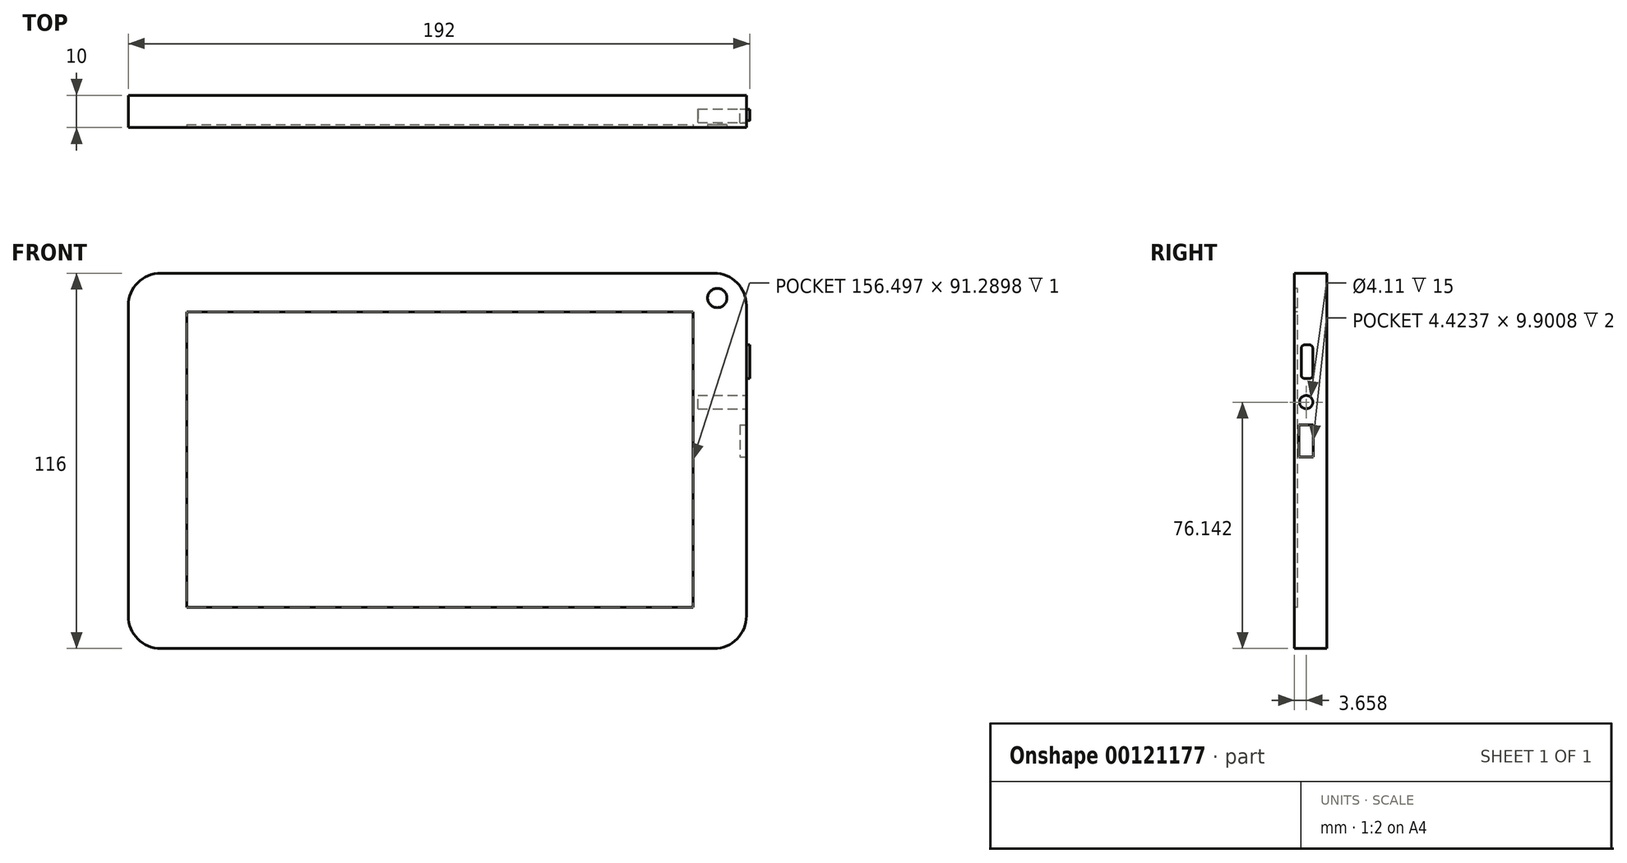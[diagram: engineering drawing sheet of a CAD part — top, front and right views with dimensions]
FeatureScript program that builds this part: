
annotation { "Feature Type Name" : "Feature", "Feature Type Description" : "" }
export const myFeature = defineFeature(function(context is Context, id is Id, definition is map)
    precondition{}
    {
        {
            var Q0;
            Q0=qCreatedBy(makeId("Front.planeOp"),FACE);
            var sketch = newSketch(context, id + "F0", { "sketchPlane" : qUnion([Q0])});
            skLineSegment(sketch, "E0.bottom", {"start": v(-85.5, 58) * mm, "end": v(85.5, 58) * mm});
            skLineSegment(sketch, "E0.top", {"start": v(-85.5, -58) * mm, "end": v(85.5, -58) * mm});
            skLineSegment(sketch, "E0.left", {"start": v(-95.5, 48) * mm, "end": v(-95.5, -48) * mm});
            skLineSegment(sketch, "E0.right", {"start": v(95.5, 48) * mm, "end": v(95.5, -48) * mm});
            skPoint(sketch, "E0.middle", {"position": v(0, 0) * mm});
            skPoint(sketch, "E1.visualSharp", {"position": v(-95.5, 58) * mm});
            skArc(sketch, "E1.filletArc", {"start": v(-85.5, 58) * mm, "mid": v(-92.57, 55.07) * mm, "end": v(-95.5, 48) * mm});
            skPoint(sketch, "E2.visualSharp", {"position": v(-95.5, -58) * mm});
            skArc(sketch, "E2.filletArc", {"start": v(-95.5, -48) * mm, "mid": v(-92.57, -55.07) * mm, "end": v(-85.5, -58) * mm});
            skPoint(sketch, "E3.visualSharp", {"position": v(95.5, -58) * mm});
            skArc(sketch, "E3.filletArc", {"start": v(85.5, -58) * mm, "mid": v(92.57, -55.07) * mm, "end": v(95.5, -48) * mm});
            skPoint(sketch, "E4.visualSharp", {"position": v(95.5, 58) * mm});
            skArc(sketch, "E4.filletArc", {"start": v(95.5, 48) * mm, "mid": v(92.57, 55.07) * mm, "end": v(85.5, 58) * mm});
            skSolve(sketch);
        }
        {
            var Q0;
            Q0=makeQuery(id+"F0.imprint","IMPRINT",FACE,{"disambiguationData":[TD([[makeQuery(id+"F0.imprint","IMPRINT",EDGE,{"derivedFrom":sQuery(id+"F0.wireOp",EDGE,"E0.bottom")}),-1.0]])]});
            extrude(context, id + "F1", {"entities" : qUnion([Q0]), "endBound" : BoundingType.SYMMETRIC, "depth" : 10 * mm});
        }
        {
            var Q0;
            Q0=makeQuery(id+"F1.opExtrude","CAP_FACE",FACE,{"disambiguationData":[OSD([sQuery(id+"F0.wireOp",EDGE,"E0.bottom"),sQuery(id+"F0.wireOp",EDGE,"E0.top"),sQuery(id+"F0.wireOp",EDGE,"E0.left"),sQuery(id+"F0.wireOp",EDGE,"E0.right"),sQuery(id+"F0.wireOp",EDGE,"E1.filletArc"),sQuery(id+"F0.wireOp",EDGE,"E2.filletArc"),sQuery(id+"F0.wireOp",EDGE,"E3.filletArc"),sQuery(id+"F0.wireOp",EDGE,"E4.filletArc")])],"isStart":false});
            var sketch = newSketch(context, id + "F2", { "sketchPlane" : qUnion([Q0])});
            skPoint(sketch, "E5.secondSnap0", {"position": v(92.57, 55.07) * mm});
            skLineSegment(sketch, "E6.bottom", {"start": v(-77.5, -45.31) * mm, "end": v(79, -45.31) * mm});
            skLineSegment(sketch, "E6.top", {"start": v(-77.5, 45.98) * mm, "end": v(79, 45.98) * mm});
            skLineSegment(sketch, "E6.left", {"start": v(-77.5, -45.31) * mm, "end": v(-77.5, 45.98) * mm});
            skLineSegment(sketch, "E6.right", {"start": v(79, -45.31) * mm, "end": v(79, 45.98) * mm});
            skCircle(sketch, "E7", {"center": v(86.5, 50.34) * mm, "radius": 2.99 * mm});
            skSolve(sketch);
        }
        {
            var Q0;
            Q0 = qSketchRegion(id + "F2", true);
            extrude(context, id + "F3", {"entities" : qUnion([Q0]), "operationType" : NewBodyOperationType.REMOVE, "oppositeDirection" : true, "depth" : 1 * mm});
        }
        {
            var Q0;
            Q0 = qSketchRegion(id + "F2", true);
            extrude(context, id + "F4", {"entities" : qUnion([Q0]), "operationType" : NewBodyOperationType.REMOVE, "oppositeDirection" : true, "depth" : 1 * mm});
        }
        {
            var Q0;
            Q0=makeQuery(id+"F1.opExtrude","SWEPT_FACE",FACE,{"disambiguationData":[OSD([sQuery(id+"F0.wireOp",EDGE,"E0.right")])]});
            var sketch = newSketch(context, id + "F5", { "sketchPlane" : qUnion([Q0])});
            skLineSegment(sketch, "E8.bottom", {"start": v(-1.83, 35.82) * mm, "end": v(-0.3, 35.82) * mm});
            skLineSegment(sketch, "E8.top", {"start": v(-1.83, 25.45) * mm, "end": v(-0.3, 25.45) * mm});
            skLineSegment(sketch, "E8.left", {"start": v(-2.83, 34.82) * mm, "end": v(-2.83, 26.45) * mm});
            skLineSegment(sketch, "E8.right", {"start": v(0.7, 34.82) * mm, "end": v(0.7, 26.45) * mm});
            skPoint(sketch, "E9.visualSharp", {"position": v(-2.83, 35.82) * mm});
            skArc(sketch, "E9.filletArc", {"start": v(-1.83, 35.82) * mm, "mid": v(-2.54, 35.53) * mm, "end": v(-2.83, 34.82) * mm});
            skPoint(sketch, "E10.visualSharp", {"position": v(0.7, 35.82) * mm});
            skArc(sketch, "E10.filletArc", {"start": v(0.7, 34.82) * mm, "mid": v(0.4, 35.53) * mm, "end": v(-0.3, 35.82) * mm});
            skPoint(sketch, "E11.visualSharp", {"position": v(-2.83, 25.45) * mm});
            skArc(sketch, "E11.filletArc", {"start": v(-2.83, 26.45) * mm, "mid": v(-2.54, 25.74) * mm, "end": v(-1.83, 25.45) * mm});
            skPoint(sketch, "E12.visualSharp", {"position": v(0.7, 25.45) * mm});
            skArc(sketch, "E12.filletArc", {"start": v(-0.3, 25.45) * mm, "mid": v(0.4, 25.74) * mm, "end": v(0.7, 26.45) * mm});
            skSolve(sketch);
        }
        {
            var Q0;
            Q0 = qSketchRegion(id + "F5", true);
            extrude(context, id + "F6", {"entities" : qUnion([Q0]), "operationType" : NewBodyOperationType.ADD, "depth" : 1 * mm});
        }
        {
            var Q0;
            Q0=makeQuery(id+"F5.imprint","IMPRINT",FACE,{"disambiguationData":[TD([[makeQuery(id+"F5.imprint","IMPRINT",EDGE,{"derivedFrom":sQuery(id+"F5.wireOp",EDGE,"E8.bottom")}),1.0]])]});
            var sketch = newSketch(context, id + "F7", { "sketchPlane" : qUnion([Q0])});
            skCircle(sketch, "E13", {"center": v(-1.34, 18.14) * mm, "radius": 2.05 * mm});
            skSolve(sketch);
        }
        {
            var Q0;
            Q0 = qSketchRegion(id + "F7", true);
            extrude(context, id + "F8", {"entities" : qUnion([Q0]), "operationType" : NewBodyOperationType.REMOVE, "oppositeDirection" : true, "depth" : 15 * mm});
        }
        {
            var Q0;
            Q0=makeQuery(id+"F5.imprint","IMPRINT",FACE,{"disambiguationData":[TD([[makeQuery(id+"F5.imprint","IMPRINT",EDGE,{"derivedFrom":sQuery(id+"F5.wireOp",EDGE,"E8.bottom")}),1.0]])]});
            var sketch = newSketch(context, id + "F9", { "sketchPlane" : qUnion([Q0])});
            skLineSegment(sketch, "E14.bottom", {"start": v(-3.32, 11.01) * mm, "end": v(0.8, 11.01) * mm});
            skLineSegment(sketch, "E14.top", {"start": v(-3.32, 1.11) * mm, "end": v(0.8, 1.11) * mm});
            skLineSegment(sketch, "E14.left", {"start": v(-3.32, 11.01) * mm, "end": v(-3.32, 1.11) * mm});
            skLineSegment(sketch, "E14.right", {"start": v(0.8, 11.01) * mm, "end": v(0.8, 1.11) * mm});
            skSolve(sketch);
        }
        {
            var Q0;
            Q0 = qSketchRegion(id + "F9", true);
            extrude(context, id + "F10", {"entities" : qUnion([Q0]), "operationType" : NewBodyOperationType.REMOVE, "depth" : 2 * mm});
        }
        {
            var Q0;
            Q0=makeQuery(id+"F5.imprint","IMPRINT",FACE,{"disambiguationData":[TD([[makeQuery(id+"F5.imprint","IMPRINT",EDGE,{"derivedFrom":sQuery(id+"F5.wireOp",EDGE,"E8.bottom")}),1.0]])]});
            var sketch = newSketch(context, id + "F11", { "sketchPlane" : qUnion([Q0])});
            skLineSegment(sketch, "E15.bottom", {"start": v(-3.6, 11.06) * mm, "end": v(0.82, 11.06) * mm});
            skLineSegment(sketch, "E15.top", {"start": v(-3.6, 1.16) * mm, "end": v(0.82, 1.16) * mm});
            skLineSegment(sketch, "E15.left", {"start": v(-3.6, 11.06) * mm, "end": v(-3.6, 1.16) * mm});
            skLineSegment(sketch, "E15.right", {"start": v(0.82, 11.06) * mm, "end": v(0.82, 1.16) * mm});
            skSolve(sketch);
        }
        {
            var Q0;
            Q0 = qSketchRegion(id + "F11", true);
            extrude(context, id + "F12", {"entities" : qUnion([Q0]), "operationType" : NewBodyOperationType.REMOVE, "oppositeDirection" : true, "depth" : 2 * mm});
        }
    });
